# Revit family: Haworth_Cappellini_Mush_SideTable_EU_PRELIMINARY
name_source: partatom
category: Furniture
revit_build: Autodesk Revit 2018 (Build: 20170223_1515(x64)
units: mm (PartAtom-declared; Revit-internal decimal feet)

## family parameters
Always vertical = Yes
Cut with Voids When Loaded = No
OmniClass Number = 23.40.20.00
OmniClass Title = General Furniture and Specialties
Room Calculation Point = No
Shared = No
Work Plane-Based = No

## types (4) — shared parameters
Actual Depth = 50 cm
Actual Diameter = 25 cm
Actual Width = 50 cm
Assembly Code = E2020200
Base Finish = Haworth _ Paint _ Undecided _ Table
Description = Haworth - Cappellini - Mush - Side Table
Manufacturer = Haworth
Max. Height = 47 cm
Min. Height = 31 cm
Model = MU_XX
Size = Verify Final Dim. w/ Haworth
Standard Height = 31, 32, 46, 47 cm
URL = https://www.haworth.com
URL - Product = https://www.haworth.com
Version = 1
Warranty = http://www.haworth.com

## per-type parameters (varying)
| type | Actual Height | Height | Thickness | Under Surface |
| MU_2M | 46 cm | 46 cm | 0 cm | No |
| MU_2R | 47 cm | 47 cm | 1 cm | Yes |
| MU_1R | 32 cm | 32 cm | 1 cm | Yes |
| MU_1M | 31 cm | 31 cm | 0 cm | No |

## geometry (parser evidence)
native form markers: Sweep x2
no freeform markers — native parametric forms only
